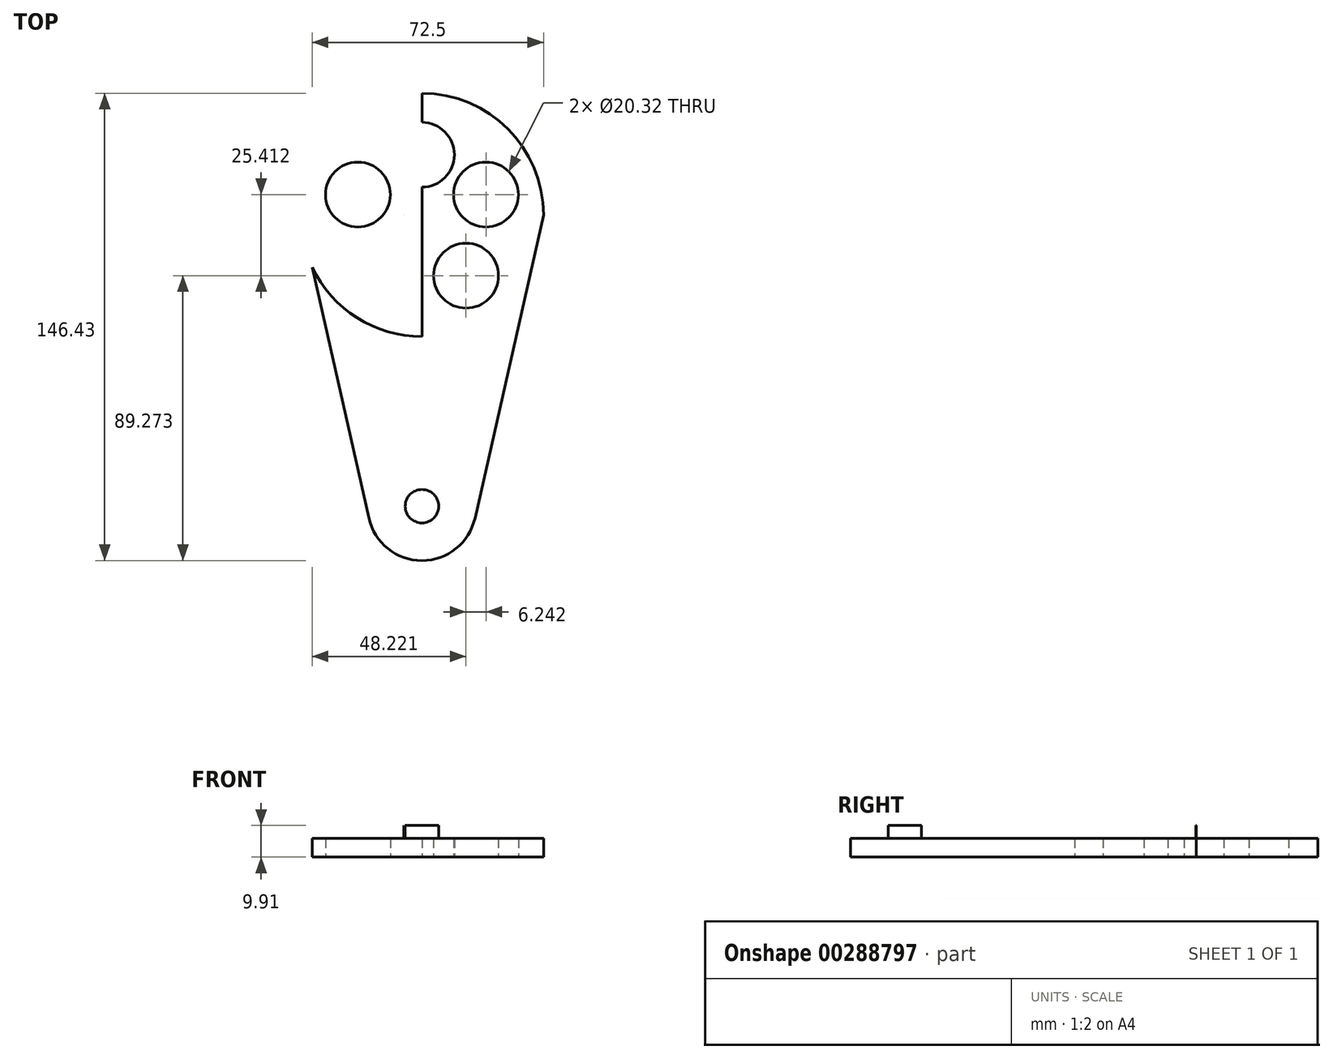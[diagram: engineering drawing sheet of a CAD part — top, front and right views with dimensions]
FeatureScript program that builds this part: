
annotation { "Feature Type Name" : "Feature", "Feature Type Description" : "" }
export const myFeature = defineFeature(function(context is Context, id is Id, definition is map)
    precondition{}
    {
        {
            var Q0;
            Q0=qCreatedBy(makeId("Top.planeOp"),FACE);
            var sketch = newSketch(context, id + "F0", { "sketchPlane" : qUnion([Q0])});
            skCircle(sketch, "E0", {"center": v(0, 0) * mm, "radius": 38.1 * mm});
            skLineSegment(sketch, "E1", {"start": v(-38.1, 0) * mm, "end": v(-16.63, -95.04) * mm});
            skLineSegment(sketch, "E2.MirrorCS", {"start": v(38.1, 0) * mm, "end": v(16.63, -95.04) * mm});
            skArc(sketch, "E3", {"start": v(-16.63, -95.04) * mm, "mid": v(0, -108.33) * mm, "end": v(16.63, -95.04) * mm});
            skLineSegment(sketch, "E4", {"start": v(0, 38.1) * mm, "end": v(0, -38.1) * mm});
            skCircle(sketch, "E5", {"center": v(20.06, 6.35) * mm, "radius": 10.16 * mm});
            skCircle(sketch, "E6", {"center": v(13.82, -19.06) * mm, "radius": 10.16 * mm});
            skCircle(sketch, "E7.MirrorC", {"center": v(-20.06, 6.35) * mm, "radius": 10.16 * mm});
            skCircle(sketch, "E8.MirrorC", {"center": v(-13.82, -19.06) * mm, "radius": 10.16 * mm});
            skCircle(sketch, "E9", {"center": v(0, 18.84) * mm, "radius": 10.16 * mm});
            skSolve(sketch);
        }
        {
            var Q0;
            Q0=makeQuery(id+"F0.imprint","IMPRINT",FACE,{"disambiguationData":[TD([[makeQuery(id+"F0.imprint","IMPRINT",EDGE,{"derivedFrom":sQuery(id+"F0.wireOp",EDGE,"E7.MirrorC")}),1.0]])]});
            var Q1;
            Q1=makeQuery(id+"F0.imprint","IMPRINT",FACE,{"disambiguationData":[TD([[makeQuery(id+"F0.imprint","IMPRINT",EDGE,{"derivedFrom":sQuery(id+"F0.wireOp",EDGE,"E5")}),-1.0]])]});
            extrude(context, id + "F1", {"entities" : qUnion([Q0, Q1]), "depth" : 5.84 * mm});
        }
        {
            var Q0;
            {var subQ0=sQuery(id+"F0.wireOp",EDGE,"E3");Q0=makeQuery(id+"F0.imprint","IMPRINT",FACE,{"disambiguationData":[TD([[makeQuery(id+"F0.imprint","IMPRINT",EDGE,{"derivedFrom":subQ0}),1.0]])]});}
            extrude(context, id + "F2", {"entities" : qUnion([Q0]), "operationType" : NewBodyOperationType.ADD, "depth" : 5.84 * mm});
        }
        {
            var Q0;
            {var subQ0=sQuery(id+"F0.wireOp",EDGE,"E2.MirrorCS");var subQ1=sQuery(id+"F0.wireOp",EDGE,"E1");var subQ2=sQuery(id+"F0.wireOp",EDGE,"E0");Q0=makeQuery(id+"F2.boolean.opBoolean","MERGE",FACE,{"derivedFrom":[makeQuery(id+"F1.opExtrude","CAP_FACE",FACE,{"disambiguationData":[OSD([subQ2,subQ1,subQ0,sQuery(id+"F0.wireOp",EDGE,"E5"),sQuery(id+"F0.wireOp",EDGE,"E6"),sQuery(id+"F0.wireOp",EDGE,"E7.MirrorC"),sQuery(id+"F0.wireOp",EDGE,"E8.MirrorC"),sQuery(id+"F0.wireOp",EDGE,"E9")])],"isStart":false}),makeQuery(id+"F2.opExtrude","CAP_FACE",FACE,{"disambiguationData":[OSD([subQ2,subQ1,subQ0,sQuery(id+"F0.wireOp",EDGE,"E3")])],"isStart":false})]});}
            var sketch = newSketch(context, id + "F3", { "sketchPlane" : qUnion([Q0])});
            skCircle(sketch, "E10", {"center": v(0, 0) * mm, "radius": 5.61 * mm});
            skCircle(sketch, "E11", {"center": v(0, -91.28) * mm, "radius": 5.23 * mm});
            skLineSegment(sketch, "E12", {"start": v(-5.61, 0) * mm, "end": v(-5.23, -91.3) * mm});
            skLineSegment(sketch, "E13", {"start": v(5.61, 0) * mm, "end": v(5.23, -91.3) * mm});
            skSolve(sketch);
        }
        {
            var Q0;
            {var subQ0=sQuery(id+"F3.wireOp",EDGE,"E11");var subQ1=makeQuery(id+"F3.imprint","INTERSECT",VERTEX,{"derivedFrom":[subQ0,sQuery(id+"F3.wireOp",EDGE,"E12")]});Q0=makeQuery(id+"F3.imprint","IMPRINT",FACE,{"disambiguationData":[TD([[makeQuery(id+"F3.imprint","IMPRINT",EDGE,{"disambiguationData":[TD([[subQ1,1.0]])],"derivedFrom":subQ0}),1.0]])]});}
            var Q1;
            {var subQ0=sQuery(id+"F3.wireOp",EDGE,"E12");var subQ5=sQuery(id+"F3.wireOp",EDGE,"E10");var subQ6=makeQuery(id+"F3.imprint","INTERSECT",VERTEX,{"disambiguationData":[OD(1.0)],"derivedFrom":[subQ5,subQ0]});Q1=makeQuery(id+"F3.imprint","IMPRINT",FACE,{"disambiguationData":[TD([[makeQuery(id+"F3.imprint","IMPRINT",EDGE,{"disambiguationData":[TD([[subQ6,-1.0]])],"derivedFrom":subQ5}),-1.0]])]});}
            var Q2;
            {var subQ0=sQuery(id+"F3.wireOp",EDGE,"E12");var subQ1=sQuery(id+"F3.wireOp",EDGE,"E10");var subQ2=makeQuery(id+"F3.imprint","INTERSECT",VERTEX,{"disambiguationData":[OD(0.0)],"derivedFrom":[subQ1,subQ0]});Q2=makeQuery(id+"F3.imprint","IMPRINT",FACE,{"disambiguationData":[TD([[makeQuery(id+"F3.imprint","IMPRINT",EDGE,{"disambiguationData":[TD([[subQ2,1.0]])],"derivedFrom":subQ1}),1.0]])]});}
            extrude(context, id + "F4", {"entities" : qUnion([Q0, Q1, Q2]), "operationType" : NewBodyOperationType.ADD, "depth" : 4.06 * mm});
        }
    });
